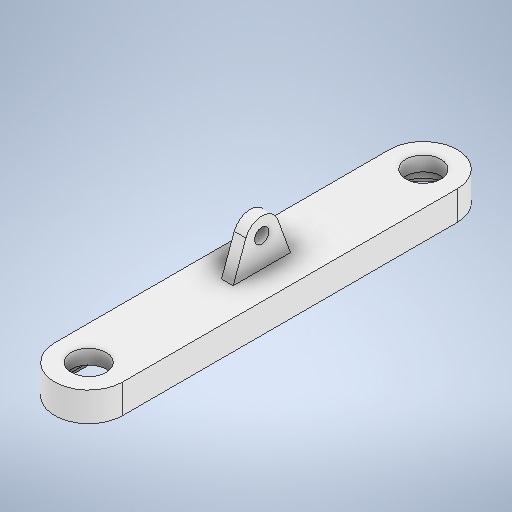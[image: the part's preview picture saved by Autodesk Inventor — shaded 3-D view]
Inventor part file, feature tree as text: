
AUTODESK INVENTOR PART (.ipt)
format: ipt  version: 2025.2 (Build 292293000, 293)  size: 310,784 bytes
history: native  units: mm
features: sketch x6, extrude x3, fillet x1, sweep x1, projected_geometry x1
ambient origin geometry x8: Origin, YZ Plane, XZ Plane, XY Plane, X Axis, Y Axis, Z Axis, Center Point
bodies: Solid1 (feature_tree)
feature tree (12):
  extrude  "Extrusion1"  Depth=69.0mm
  extrude  "Extrusion2"  Depth=14.0mm
  fillet  "Fillet1"  Radius=6.0mm
  extrude  "Extrusion5"  Depth=2.4mm TaperAngle=0.0deg
  sketch  "Sketch7"  dims[d10=7.0mm d11=3.490659mm]
  sweep  "Sweep1"
  sketch  "Sketch1"  dims[d0=7.2mm d1=69.0mm]
  sketch  "Sketch2"  dims[d2=83.0mm d3=14.0mm d4=6.0mm d5=0.0mm]
  sketch  "Sketch5"  dims[d6=7.0mm d8=2.4mm d9=0.0mm]
  projected_geometry  "Projected Loop1"
  sketch  "Sketch8"  dims[d12=6.0mm d13=3.0mm d32=1.5mm d33=3.0mm d34=0.0mm d38=1.0mm d39=45.0deg d40=0.0mm d41=0.0mm d42=0.5mm d14=0.872665mm d36=0.5mm d37=0.872665mm]
  sketch  "3D Sketch1"
